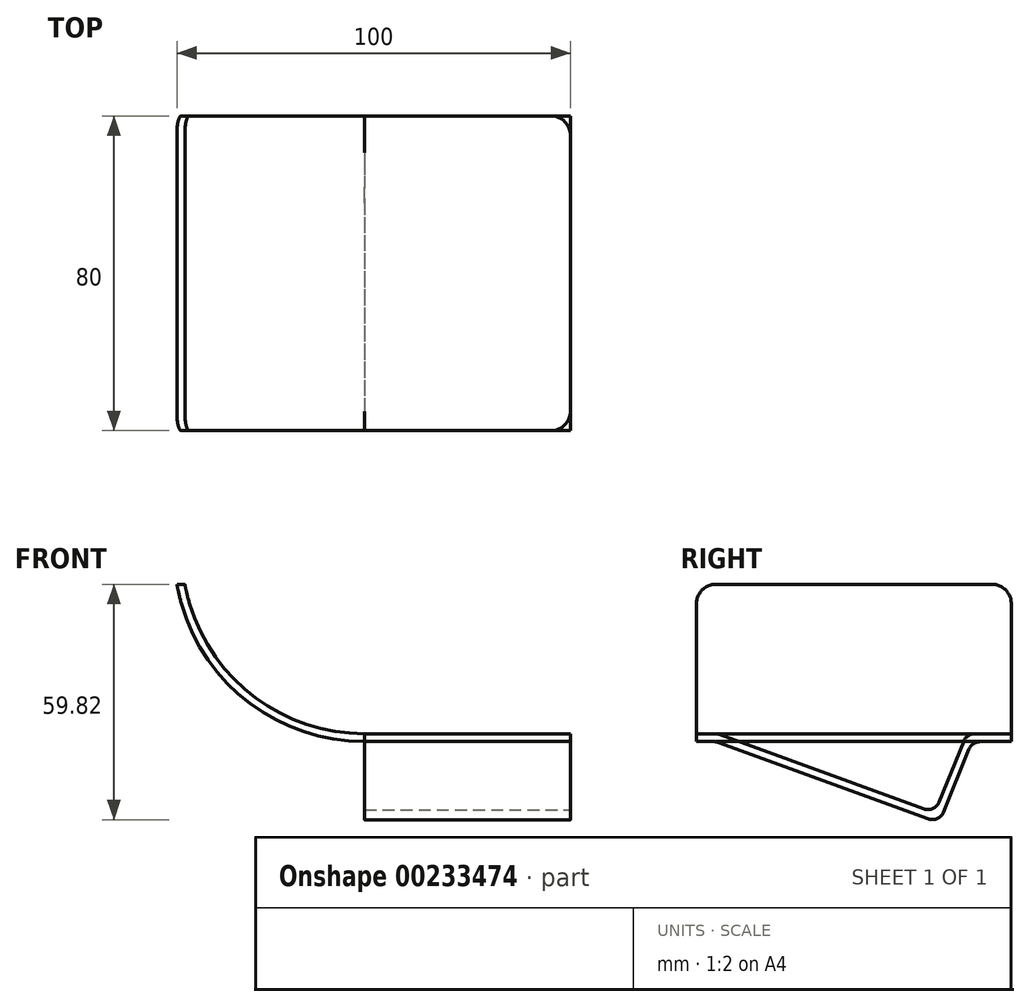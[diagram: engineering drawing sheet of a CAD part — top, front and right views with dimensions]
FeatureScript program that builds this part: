
annotation { "Feature Type Name" : "Feature", "Feature Type Description" : "" }
export const myFeature = defineFeature(function(context is Context, id is Id, definition is map)
    precondition{}
    {
        {
            var Q0;
            Q0=qCreatedBy(makeId("Front.planeOp"),FACE);
            var sketch = newSketch(context, id + "F0", { "sketchPlane" : qUnion([Q0])});
            skLineSegment(sketch, "E0", {"start": v(0, 0) * mm, "end": v(-52.33, 0) * mm});
            skLineSegment(sketch, "E1", {"start": v(-100, 40) * mm, "end": v(-103.8, 61.59) * mm, "construction": true});
            skArc(sketch, "E2", {"start": v(-52.33, 0) * mm, "mid": v(-83.44, 11.32) * mm, "end": v(-100, 40) * mm});
            skLineSegment(sketch, "E3", {"start": v(0, 0) * mm, "end": v(0, 20.65) * mm, "construction": true});
            skArc(sketch, "E4.0", {"start": v(-52.33, 2) * mm, "mid": v(-82.02, 12.74) * mm, "end": v(-97.97, 40) * mm});
            skLineSegment(sketch, "E4.1", {"start": v(0, 2) * mm, "end": v(-52.33, 2) * mm});
            skLineSegment(sketch, "E5", {"start": v(-100, 40) * mm, "end": v(-97.97, 40) * mm});
            skLineSegment(sketch, "E6", {"start": v(0, 2) * mm, "end": v(0, 0) * mm});
            skLineSegment(sketch, "E7", {"start": v(25.03, -0.7) * mm, "end": v(25.03, 27.63) * mm, "construction": true});
            skLineSegment(sketch, "E8.MirrorCS", {"start": v(50.06, 2) * mm, "end": v(102.4, 2) * mm, "construction": true});
            skArc(sketch, "E9.MirrorCS", {"start": v(102.4, 2) * mm, "mid": v(132.09, 12.74) * mm, "end": v(148.03, 40) * mm, "construction": true});
            skArc(sketch, "E10.MirrorCS", {"start": v(102.4, 0) * mm, "mid": v(133.5, 11.32) * mm, "end": v(150.06, 40) * mm, "construction": true});
            skLineSegment(sketch, "E11.MirrorCS", {"start": v(50.06, 0) * mm, "end": v(102.4, 0) * mm, "construction": true});
            skLineSegment(sketch, "E12.MirrorCS", {"start": v(150.06, 40) * mm, "end": v(148.03, 40) * mm, "construction": true});
            skLineSegment(sketch, "E13", {"start": v(50.06, 2) * mm, "end": v(50.06, 0) * mm, "construction": true});
            skLineSegment(sketch, "E14", {"start": v(-44.97, 38.96) * mm, "end": v(-44.97, -14.07) * mm, "construction": true});
            skLineSegment(sketch, "E15", {"start": v(95.03, 40.11) * mm, "end": v(95.03, -16.87) * mm, "construction": true});
            skSolve(sketch);
        }
        {
            var Q0;
            Q0 = qSketchRegion(id + "F0", true);
            extrude(context, id + "F1", {"entities" : qUnion([Q0]), "offsetDistance" : 25 * mm, "depth" : 80 * mm});
        }
        {
            var Q0;
            Q0=makeQuery(id+"F1.opExtrude","CAP_EDGE",EDGE,{"disambiguationData":[OSD([sQuery(id+"F0.wireOp",EDGE,"E5")])],"isStart":false});
            var Q1;
            Q1=makeQuery(id+"F1.opExtrude","CAP_EDGE",EDGE,{"disambiguationData":[OSD([sQuery(id+"F0.wireOp",EDGE,"E5")])],"isStart":true});
            var Q2;
            Q2=makeQuery(id+"F1.opExtrude","CAP_EDGE",EDGE,{"disambiguationData":[OSD([sQuery(id+"F0.wireOp",EDGE,"E6")])],"isStart":false});
            var Q3;
            Q3=makeQuery(id+"F1.opExtrude","CAP_EDGE",EDGE,{"disambiguationData":[OSD([sQuery(id+"F0.wireOp",EDGE,"E6")])],"isStart":true});
            fillet(context, id + "F2", {"entities" : qUnion([Q0, Q1, Q2, Q3]), "radius" : 5 * mm, "tangentPropagation" : true, "allowEdgeOverflow" : false});
        }
        {
            var Q0;
            Q0=qCreatedBy(makeId("Right.planeOp"),FACE);
            var sketch = newSketch(context, id + "F3", { "sketchPlane" : qUnion([Q0])});
            skLineSegment(sketch, "E16", {"start": v(-74.5, -0.18) * mm, "end": v(-21.06, -19.63) * mm});
            skLineSegment(sketch, "E17", {"start": v(-17.25, -17.94) * mm, "end": v(-10.76, -1.88) * mm});
            skLineSegment(sketch, "E18", {"start": v(-75.53, 0) * mm, "end": v(-80, 0) * mm});
            skLineSegment(sketch, "E19", {"start": v(-80, 0) * mm, "end": v(-80, 2) * mm});
            skLineSegment(sketch, "E20", {"start": v(-80, 2) * mm, "end": v(-75.18, 2) * mm});
            skLineSegment(sketch, "E21", {"start": v(-74.15, 1.82) * mm, "end": v(-22.19, -17.1) * mm});
            skLineSegment(sketch, "E22", {"start": v(-18.38, -15.4) * mm, "end": v(-12.1, 0.12) * mm});
            skLineSegment(sketch, "E23", {"start": v(-9.33, 2) * mm, "end": v(0, 2) * mm});
            skLineSegment(sketch, "E24", {"start": v(0, 2) * mm, "end": v(0, 0) * mm});
            skLineSegment(sketch, "E25", {"start": v(0, 0) * mm, "end": v(-7.98, 0) * mm});
            skPoint(sketch, "E26.visualSharp", {"position": v(-10, 0) * mm});
            skArc(sketch, "E26.filletArc", {"start": v(-7.98, 0) * mm, "mid": v(-9.65, -0.51) * mm, "end": v(-10.76, -1.88) * mm});
            skPoint(sketch, "E27.visualSharp", {"position": v(-11.35, 2) * mm});
            skArc(sketch, "E27.filletArc", {"start": v(-9.33, 2) * mm, "mid": v(-11, 1.49) * mm, "end": v(-12.1, 0.12) * mm});
            skPoint(sketch, "E28.visualSharp", {"position": v(-74.65, 2) * mm});
            skArc(sketch, "E28.filletArc", {"start": v(-74.15, 1.82) * mm, "mid": v(-74.66, 1.95) * mm, "end": v(-75.18, 2) * mm});
            skPoint(sketch, "E29.visualSharp", {"position": v(-75, 0) * mm});
            skArc(sketch, "E29.filletArc", {"start": v(-74.5, -0.18) * mm, "mid": v(-75, -0.05) * mm, "end": v(-75.53, 0) * mm});
            skPoint(sketch, "E30.visualSharp", {"position": v(-19.46, -18.09) * mm});
            skArc(sketch, "E30.filletArc", {"start": v(-22.19, -17.1) * mm, "mid": v(-19.94, -17.02) * mm, "end": v(-18.38, -15.4) * mm});
            skPoint(sketch, "E31.visualSharp", {"position": v(-18.33, -20.63) * mm});
            skArc(sketch, "E31.filletArc", {"start": v(-21.06, -19.63) * mm, "mid": v(-18.8, -19.56) * mm, "end": v(-17.25, -17.94) * mm});
            skSolve(sketch);
        }
        {
            var Q0;
            Q0=qCreatedBy(makeId("Right.planeOp"),FACE);
            var Q1;
            Q1=makeQuery(id+"F1.opExtrude","CAP_VERTEX",VERTEX,{"disambiguationData":[OSD([sQuery(id+"F0.wireOp",EDGE,"E4.0"),sQuery(id+"F0.wireOp",EDGE,"E4.1")])],"isStart":true});
            cPlane(context, id + "F4", {"entities" : qUnion([Q0, Q1]), "cplaneType" : CPlaneType.PLANE_POINT, "offset" : 25 * mm, "width" : 150 * mm, "height" : 150 * mm});
        }
        {
            var Q0;
            Q0 = qSketchRegion(id + "F3", true);
            var Q1;
            Q1=qCreatedBy(id+"F4.planeOp",FACE);
            extrude(context, id + "F5", {"entities" : qUnion([Q0]), "endBound" : BoundingType.UP_TO_SURFACE, "oppositeDirection" : true, "depth" : 25 * mm, "endBoundEntityFace" : qUnion([Q1]), "offsetDistance" : 25 * mm});
        }
    });
